# Revit family: Plumbing-Urinals-Combos-Sloan-Valve-WEUS-10001201
name_source: partatom
category: Plumbing Fixtures
units: mm (PartAtom-declared; Revit-internal decimal feet)

## family parameters
Cut with Voids When Loaded = No
Host = Face
OmniClass Number = 23.45.05.21.11.21
OmniClass Title = Urinals
Part Type = Normal
Room Calculation Point = No
Round Connector Dimension = Use Diameter
Shared = No

## types (2) — shared parameters
Assembly Code = D2010
Depth = 14.25 "
Edition number = 1
Flush Rate = 0.125 GPF (0.5 LPF)
Flushometer Code = 3370010
Height = 25.5 "
Keynote = 15410
Manufacturer = Sloan Valve
Operating Water Pressure = 15 – 80 PSI (103 – 552 kPa). Specific fixtures may require greater minimum flowing pressure - consult manufacturer requirements.
Product Material = Sloan Valve - Vitreous China - White
Product data url = https://www.bimobject.com
Sanitary Drain Connection Diameter = 2"
URL = www.sloanvalve.com
Urinal Code = 1101009
Valve Pressure Drop = 0.00 psi
Water Inlet Connection Diameter = 1"
Width = 17.25 "
zero-valued in all types: CWFU, Default Elevation, WFU

## per-type parameters (varying)
| type | Description | Part Number |
| WEUS-1000.1201 | SU-1009 Urinal and SOLIS 8186 Flushometer. | 10001201 |
| WEUS-1000.1201-CO | Carbon Offset, SU-1009 Urinal and SOLIS 8186 Flushometer | 10001201T |

note: column(s) folded — value = type name in every type: Model

## geometry (parser evidence)
native form markers: Sweep x7
no freeform markers — native parametric forms only
